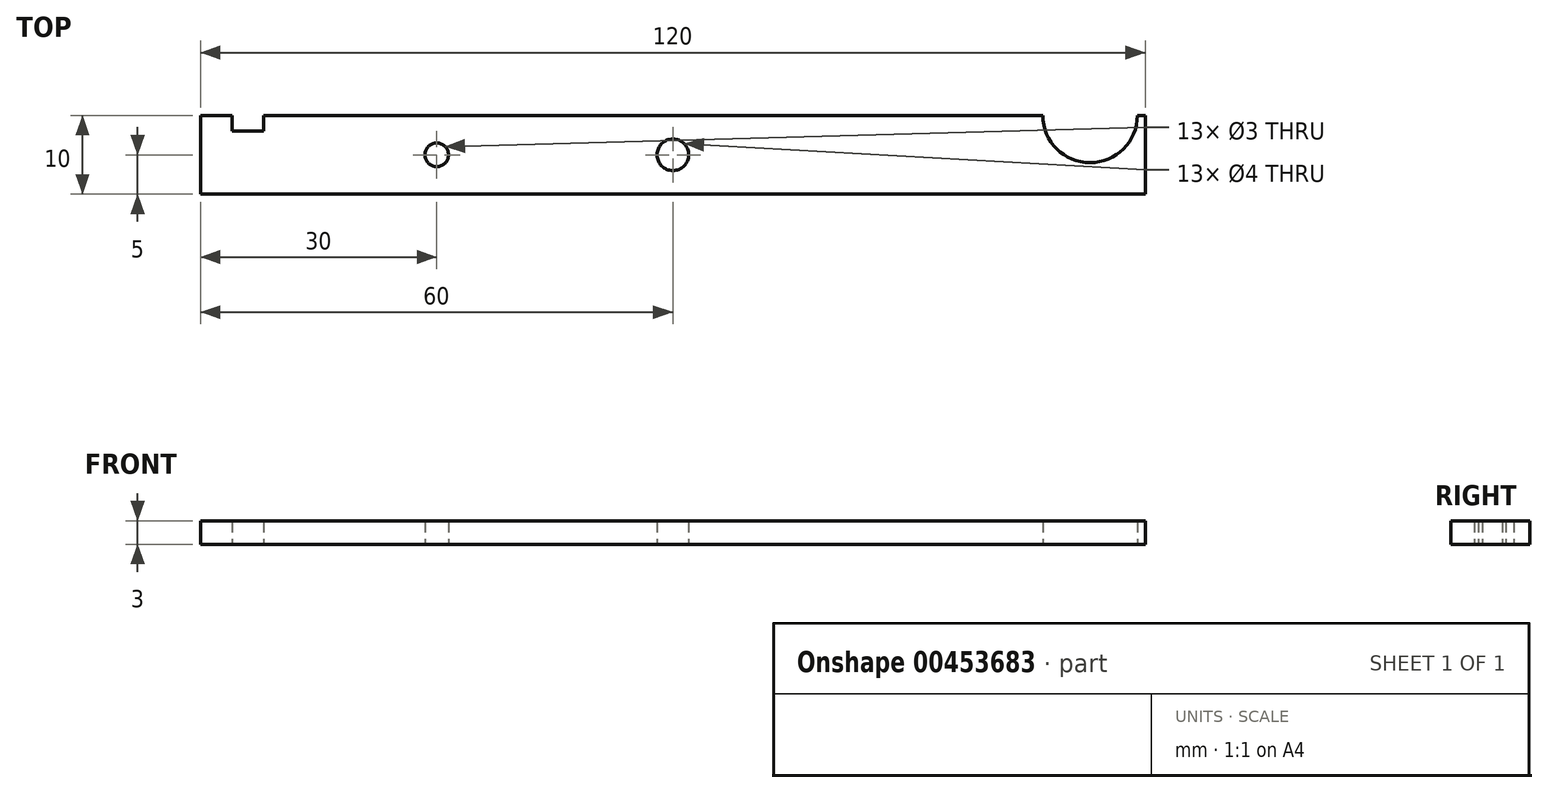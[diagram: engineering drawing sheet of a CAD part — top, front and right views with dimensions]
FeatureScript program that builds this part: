
annotation { "Feature Type Name" : "Feature", "Feature Type Description" : "" }
export const myFeature = defineFeature(function(context is Context, id is Id, definition is map)
    precondition{}
    {
        {
            var Q0;
            Q0=qCreatedBy(makeId("Top.planeOp"),FACE);
            var sketch = newSketch(context, id + "F0", { "sketchPlane" : qUnion([Q0])});
            skLineSegment(sketch, "E0.bottom", {"start": v(60, -5) * mm, "end": v(-60, -5) * mm});
            skLineSegment(sketch, "E0.top", {"start": v(60, 5) * mm, "end": v(-60, 5) * mm});
            skLineSegment(sketch, "E0.left", {"start": v(60, -5) * mm, "end": v(60, 5) * mm});
            skLineSegment(sketch, "E0.right", {"start": v(-60, -5) * mm, "end": v(-60, 5) * mm});
            skPoint(sketch, "E0.middle", {"position": v(0, 0) * mm});
            skCircle(sketch, "E1", {"center": v(0, 0) * mm, "radius": 7 * mm});
            skCircle(sketch, "E2", {"center": v(0, 0) * mm, "radius": 2 * mm});
            skLineSegment(sketch, "E3.bottom", {"start": v(-56, 5) * mm, "end": v(-52, 5) * mm});
            skLineSegment(sketch, "E3.top", {"start": v(-56, 3) * mm, "end": v(-52, 3) * mm});
            skLineSegment(sketch, "E3.left", {"start": v(-56, 5) * mm, "end": v(-56, 3) * mm});
            skLineSegment(sketch, "E3.right", {"start": v(-52, 5) * mm, "end": v(-52, 3) * mm});
            skCircle(sketch, "E4", {"center": v(53, 5) * mm, "radius": 6 * mm});
            skCircle(sketch, "E5", {"center": v(-30, 0) * mm, "radius": 1.5 * mm});
            skSolve(sketch);
        }
        {
            var Q0;
            {var subQ0=sQuery(id+"F0.wireOp",EDGE,"E0.right");Q0=makeQuery(id+"F0.imprint","IMPRINT",FACE,{"disambiguationData":[TD([[makeQuery(id+"F0.imprint","IMPRINT",EDGE,{"derivedFrom":subQ0}),-1.0]])]});}
            var Q1;
            {var subQ0=sQuery(id+"F0.wireOp",EDGE,"E0.left");Q1=makeQuery(id+"F0.imprint","IMPRINT",FACE,{"disambiguationData":[TD([[makeQuery(id+"F0.imprint","IMPRINT",EDGE,{"derivedFrom":subQ0}),1.0]])]});}
            var Q2;
            {var subQ0=sQuery(id+"F0.wireOp",EDGE,"E1");var subQ1=sQuery(id+"F0.wireOp",EDGE,"E0.top");var subQ2=makeQuery(id+"F0.imprint","INTERSECT",VERTEX,{"disambiguationData":[OD(0.0)],"derivedFrom":[subQ1,subQ0]});Q2=makeQuery(id+"F0.imprint","IMPRINT",FACE,{"disambiguationData":[TD([[makeQuery(id+"F0.imprint","IMPRINT",EDGE,{"disambiguationData":[TD([[subQ2,-1.0]])],"derivedFrom":subQ1}),-1.0]])]});}
            var Q3;
            Q3=makeQuery(id+"F0.imprint","IMPRINT",FACE,{"disambiguationData":[TD([[makeQuery(id+"F0.imprint","IMPRINT",EDGE,{"derivedFrom":sQuery(id+"F0.wireOp",EDGE,"E2")}),-1.0]])]});
            var Q4;
            {var subQ0=sQuery(id+"F0.wireOp",EDGE,"E1");var subQ1=sQuery(id+"F0.wireOp",EDGE,"E0.bottom");var subQ2=makeQuery(id+"F0.imprint","INTERSECT",VERTEX,{"disambiguationData":[OD(0.0)],"derivedFrom":[subQ1,subQ0]});Q4=makeQuery(id+"F0.imprint","IMPRINT",FACE,{"disambiguationData":[TD([[makeQuery(id+"F0.imprint","IMPRINT",EDGE,{"disambiguationData":[TD([[subQ2,-1.0]])],"derivedFrom":subQ1}),1.0]])]});}
            extrude(context, id + "F1", {"entities" : qUnion([Q0, Q1, Q2, Q3, Q4]), "depth" : 3 * mm});
        }
    });
